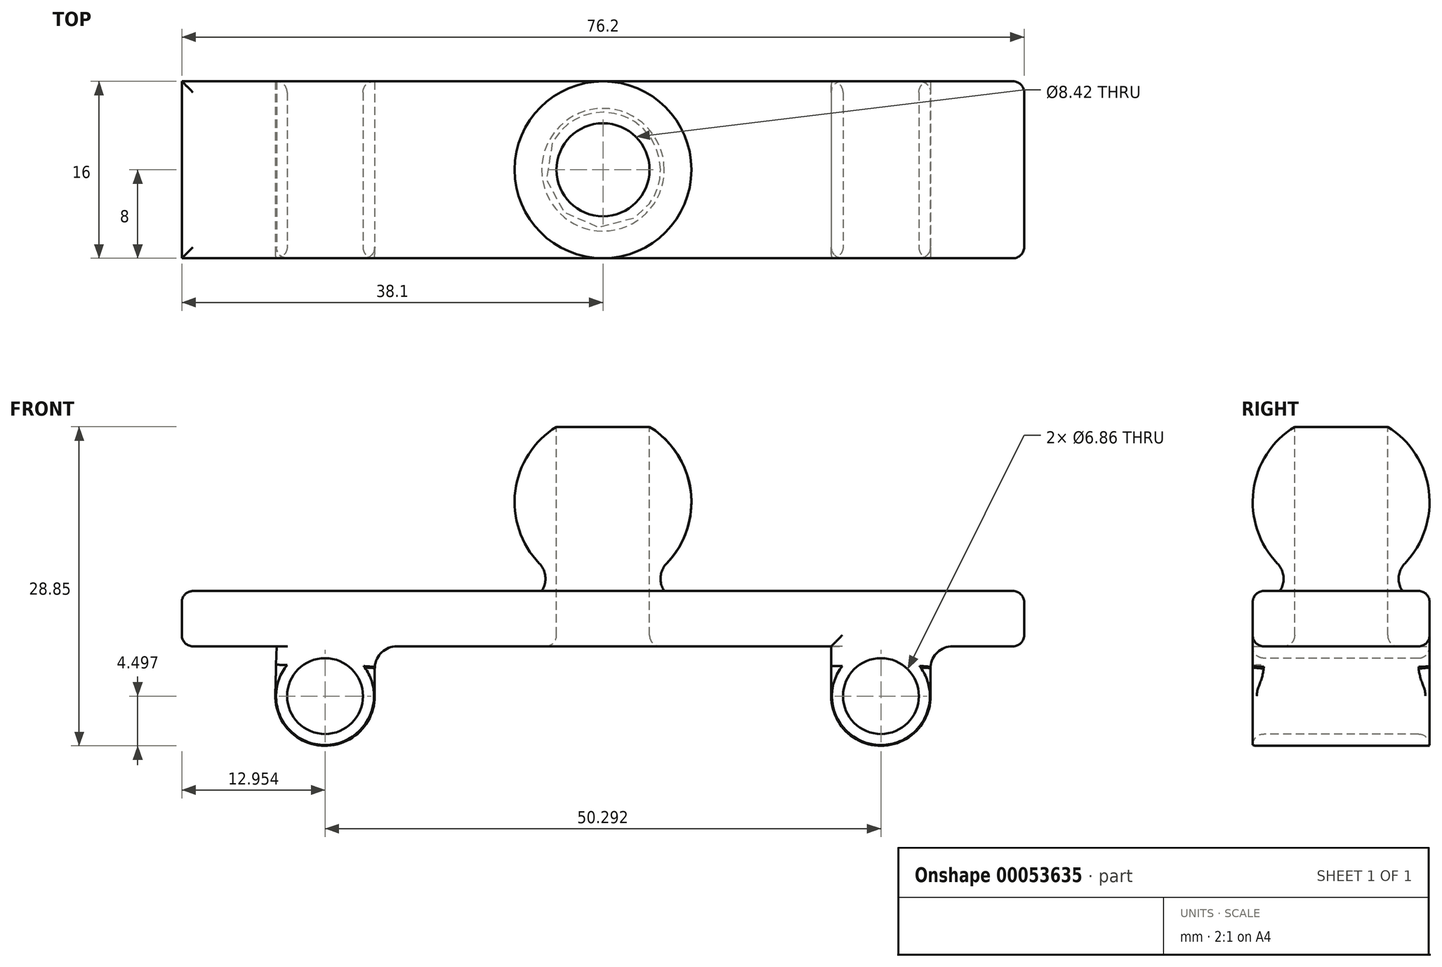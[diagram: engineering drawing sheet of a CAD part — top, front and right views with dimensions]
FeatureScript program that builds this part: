
annotation { "Feature Type Name" : "Feature", "Feature Type Description" : "" }
export const myFeature = defineFeature(function(context is Context, id is Id, definition is map)
    precondition{}
    {
        {
            var Q0;
            Q0=qCreatedBy(makeId("Front.planeOp"),FACE);
            var sketch = newSketch(context, id + "F0", { "sketchPlane" : qUnion([Q0])});
            skArc(sketch, "E0", {"start": v(0, 4.09) * mm, "mid": v(0.5, 4.1) * mm, "end": v(1, 4.15) * mm});
            skLineSegment(sketch, "E1", {"start": v(5.54, 4.04) * mm, "end": v(10.12, -2.8) * mm});
            skLineSegment(sketch, "E2", {"start": v(10.12, -2.8) * mm, "end": v(10.12, -5.91) * mm});
            skLineSegment(sketch, "E3", {"start": v(10.12, -5.91) * mm, "end": v(7.88, -5.91) * mm});
            skArc(sketch, "E4", {"start": v(7.88, -5.91) * mm, "mid": v(6.7, 0.67) * mm, "end": v(1, 4.15) * mm});
            skLineSegment(sketch, "E5", {"start": v(0, 10.09) * mm, "end": v(7.75, 10.09) * mm, "construction": true});
            skPoint(sketch, "E6", {"position": v(0, 20.09) * mm});
            skPoint(sketch, "E7", {"position": v(0, 10.09) * mm});
            skPoint(sketch, "E8.orphan", {"position": v(-7.75, 10.09) * mm});
            skPoint(sketch, "E9.orphan", {"position": v(0, -5.91) * mm});
            skLineSegment(sketch, "E10", {"start": v(0, 20.09) * mm, "end": v(0, 4.09) * mm});
            skArc(sketch, "E11.trimOffspring", {"start": v(5.76, 6.54) * mm, "mid": v(7.36, 15.22) * mm, "end": v(0, 20.09) * mm});
            skLineSegment(sketch, "E12", {"start": v(0, 4.09) * mm, "end": v(0, -5.91) * mm, "construction": true});
            skPoint(sketch, "E13.visualSharp", {"position": v(4.56, 5.5) * mm});
            skArc(sketch, "E13.filletArc", {"start": v(5.76, 6.54) * mm, "mid": v(5.21, 5.33) * mm, "end": v(5.54, 4.04) * mm});
            skSolve(sketch);
        }
        {
            var Q0;
            Q0=qSketchRegion(id+"F0",true);
            var Q1;
            Q1=sQuery(id+"F0.wireOp",EDGE,"E12");
            revolve(context, id + "F1", {"entities" : qUnion([Q0]), "axis" : qUnion([Q1]), "revolveType" : RevolveType.FULL});
        }
        {
            var Q0;
            Q0=qCreatedBy(makeId("Top.planeOp"),FACE);
            var sketch = newSketch(context, id + "F2", { "sketchPlane" : qUnion([Q0])});
            skCircle(sketch, "E14", {"center": v(0, 0) * mm, "radius": 4.2 * mm});
            skSolve(sketch);
        }
        {
            var Q0;
            Q0=qSketchRegion(id+"F2",true);
            extrude(context, id + "F3", {"entities" : qUnion([Q0]), "operationType" : NewBodyOperationType.REMOVE, "endBound" : BoundingType.SYMMETRIC, "oppositeDirection" : true, "depth" : 50 * mm});
        }
        {
            var Q0;
            Q0=qCreatedBy(makeId("Right.planeOp"),FACE);
            var sketch = newSketch(context, id + "F4", { "sketchPlane" : qUnion([Q0])});
            skLineSegment(sketch, "E15.bottom", {"start": v(1, -5.91) * mm, "end": v(-1, -5.91) * mm});
            skLineSegment(sketch, "E15.left", {"start": v(1, -5.91) * mm, "end": v(1, -0.91) * mm});
            skLineSegment(sketch, "E15.right", {"start": v(-1, -5.91) * mm, "end": v(-1, -0.91) * mm});
            skArc(sketch, "E16", {"start": v(1, -0.91) * mm, "mid": v(0, 0.09) * mm, "end": v(-1, -0.91) * mm});
            skSolve(sketch);
        }
        {
            var Q0;
            Q0=qSketchRegion(id+"F4",true);
            extrude(context, id + "F5", {"entities" : qUnion([Q0]), "operationType" : NewBodyOperationType.REMOVE, "endBound" : BoundingType.SYMMETRIC, "oppositeDirection" : true, "depth" : 25 * mm});
        }
        {
            var Q0;
            Q0=qCreatedBy(makeId("Front.planeOp"),FACE);
            var sketch = newSketch(context, id + "F6", { "sketchPlane" : qUnion([Q0])});
            skLineSegment(sketch, "E17.bottom", {"start": v(-34.6, 4.04) * mm, "end": v(25.65, 4.04) * mm});
            skLineSegment(sketch, "E17.top", {"start": v(-34.6, -16.9) * mm, "end": v(25.65, -16.9) * mm});
            skLineSegment(sketch, "E17.left", {"start": v(-34.6, 4.04) * mm, "end": v(-34.6, -16.9) * mm});
            skLineSegment(sketch, "E17.right", {"start": v(25.65, 4.04) * mm, "end": v(25.65, -16.9) * mm});
            skSolve(sketch);
        }
        {
            var Q0;
            Q0 = qSketchRegion(id + "F6", true);
            extrude(context, id + "F7", {"entities" : qUnion([Q0]), "operationType" : NewBodyOperationType.REMOVE, "endBound" : BoundingType.SYMMETRIC, "oppositeDirection" : true, "depth" : 25 * mm});
        }
        {
            var Q0;
            Q0=makeQuery(id+"F7.boolean.opBoolean","COPY",FACE,{"derivedFrom":makeQuery(id+"F7.opExtrude","SWEPT_FACE",FACE,{"disambiguationData":[OSD([sQuery(id+"F6.wireOp",EDGE,"E17.bottom")])]})});
            var sketch = newSketch(context, id + "F8", { "sketchPlane" : qUnion([Q0])});
            skLineSegment(sketch, "E18.rect.bottom", {"start": v(38.1, -8) * mm, "end": v(-38.1, -8) * mm});
            skLineSegment(sketch, "E18.rect.top", {"start": v(38.1, 8) * mm, "end": v(-38.1, 8) * mm});
            skLineSegment(sketch, "E18.rect.left", {"start": v(38.1, -8) * mm, "end": v(38.1, 8) * mm});
            skLineSegment(sketch, "E18.rect.right", {"start": v(-38.1, -8) * mm, "end": v(-38.1, 8) * mm});
            skPoint(sketch, "E18.rect.middle", {"position": v(0, 0) * mm});
            skSolve(sketch);
        }
        {
            var Q0;
            Q0 = qSketchRegion(id + "F8", true);
            extrude(context, id + "F9", {"entities" : qUnion([Q0]), "operationType" : NewBodyOperationType.ADD, "depth" : 5 * mm});
        }
        {
            var Q0;
            Q0=makeQuery(id+"F9.opExtrude","SWEPT_FACE",FACE,{"disambiguationData":[OSD([sQuery(id+"F8.wireOp",EDGE,"E18.rect.top")])]});
            var sketch = newSketch(context, id + "F10", { "sketchPlane" : qUnion([Q0])});
            skCircle(sketch, "E19", {"center": v(-25.15, -5.46) * mm, "radius": 3.43 * mm});
            skCircle(sketch, "E20", {"center": v(25.15, -5.46) * mm, "radius": 3.43 * mm});
            skLineSegment(sketch, "E21", {"start": v(-25.15, -5.46) * mm, "end": v(25.15, -5.46) * mm, "construction": true});
            skPoint(sketch, "E22", {"position": v(0, -5.46) * mm});
            skArc(sketch, "E23", {"start": v(-29.64, -5.34) * mm, "mid": v(-25.2, -9.96) * mm, "end": v(-20.65, -5.46) * mm});
            skArc(sketch, "E24", {"start": v(20.65, -5.46) * mm, "mid": v(25.16, -9.96) * mm, "end": v(29.65, -5.43) * mm});
            skLineSegment(sketch, "E25", {"start": v(-29.64, -5.34) * mm, "end": v(-29.53, -0.96) * mm});
            skLineSegment(sketch, "E26", {"start": v(-20.65, -5.46) * mm, "end": v(-20.65, -0.96) * mm});
            skLineSegment(sketch, "E27", {"start": v(20.65, -5.46) * mm, "end": v(20.65, -0.96) * mm});
            skLineSegment(sketch, "E28", {"start": v(-29.53, -0.96) * mm, "end": v(-20.65, -0.96) * mm});
            skLineSegment(sketch, "E29", {"start": v(20.65, -0.96) * mm, "end": v(29.61, -0.96) * mm});
            skLineSegment(sketch, "E30", {"start": v(29.65, -5.43) * mm, "end": v(29.61, -0.96) * mm});
            skSolve(sketch);
        }
        {
            var Q0;
            Q0 = qSketchRegion(id + "F10", true);
            extrude(context, id + "F11", {"entities" : qUnion([Q0]), "oppositeDirection" : true, "depth" : 16 * mm});
        }
        {
            var Q0;
            Q0=makeQuery(id+"F11.opExtrude","SWEPT_BODY",BODY,{"disambiguationData":[OSD([sQuery(id+"F10.wireOp",EDGE,"E19"),sQuery(id+"F10.wireOp",EDGE,"E23"),sQuery(id+"F10.wireOp",EDGE,"E25"),sQuery(id+"F10.wireOp",EDGE,"E26"),sQuery(id+"F10.wireOp",EDGE,"E28")])]});
            var Q1;
            Q1=makeQuery(id+"F1.opRevolve","SWEPT_BODY",BODY,{"disambiguationData":[OSD([sQuery(id+"F0.wireOp",EDGE,"E0"),sQuery(id+"F0.wireOp",EDGE,"E1"),sQuery(id+"F0.wireOp",EDGE,"E2"),sQuery(id+"F0.wireOp",EDGE,"E3"),sQuery(id+"F0.wireOp",EDGE,"E4"),sQuery(id+"F0.wireOp",EDGE,"E10"),sQuery(id+"F0.wireOp",EDGE,"E11.trimOffspring"),sQuery(id+"F0.wireOp",EDGE,"E13.filletArc")])]});
            booleanBodies(context, id + "F12", {"operationType" : BooleanOperationType.UNION, "tools" : qUnion([Q0, Q1])});
        }
        {
            var Q0;
            Q0=makeQuery(id+"F11.opExtrude","SWEPT_BODY",BODY,{"disambiguationData":[OSD([sQuery(id+"F10.wireOp",EDGE,"E20"),sQuery(id+"F10.wireOp",EDGE,"E24"),sQuery(id+"F10.wireOp",EDGE,"E27"),sQuery(id+"F10.wireOp",EDGE,"E29"),sQuery(id+"F10.wireOp",EDGE,"E30")])]});
            var Q1;
            Q1=makeQuery(id+"F11.opExtrude","SWEPT_BODY",BODY,{"disambiguationData":[OSD([sQuery(id+"F10.wireOp",EDGE,"E19"),sQuery(id+"F10.wireOp",EDGE,"E23"),sQuery(id+"F10.wireOp",EDGE,"E25"),sQuery(id+"F10.wireOp",EDGE,"E26"),sQuery(id+"F10.wireOp",EDGE,"E28")])]});
            booleanBodies(context, id + "F13", {"operationType" : BooleanOperationType.UNION, "tools" : qUnion([Q0, Q1])});
        }
        {
            var Q0;
            Q0=makeQuery(id+"F11.opExtrude","SWEPT_EDGE",EDGE,{"disambiguationData":[OSD([sQuery(id+"F8.wireOp",EDGE,"E18.rect.top"),sQuery(id+"F10.wireOp",EDGE,"E25"),sQuery(id+"F10.wireOp",EDGE,"E28")])]});
            var Q1;
            Q1=makeQuery(id+"F11.opExtrude","SWEPT_EDGE",EDGE,{"disambiguationData":[OSD([sQuery(id+"F8.wireOp",EDGE,"E18.rect.top"),sQuery(id+"F10.wireOp",EDGE,"E26"),sQuery(id+"F10.wireOp",EDGE,"E28")])]});
            var Q2;
            Q2=makeQuery(id+"F11.opExtrude","SWEPT_EDGE",EDGE,{"disambiguationData":[OSD([sQuery(id+"F8.wireOp",EDGE,"E18.rect.top"),sQuery(id+"F10.wireOp",EDGE,"E27"),sQuery(id+"F10.wireOp",EDGE,"E29")])]});
            var Q3;
            Q3=makeQuery(id+"F11.opExtrude","SWEPT_EDGE",EDGE,{"disambiguationData":[OSD([sQuery(id+"F8.wireOp",EDGE,"E18.rect.top"),sQuery(id+"F10.wireOp",EDGE,"E29"),sQuery(id+"F10.wireOp",EDGE,"E30")])]});
            fillet(context, id + "F14", {"entities" : qUnion([Q0, Q1, Q2, Q3]), "radius" : 2 * mm, "tangentPropagation" : true, "allowEdgeOverflow" : false});
        }
        {
            var Q0;
            Q0=makeQuery(id+"F11.opExtrude","CAP_EDGE",EDGE,{"disambiguationData":[OSD([sQuery(id+"F10.wireOp",EDGE,"E20")])],"isStart":false});
            var Q1;
            Q1=makeQuery(id+"F11.opExtrude","CAP_EDGE",EDGE,{"disambiguationData":[OSD([sQuery(id+"F10.wireOp",EDGE,"E19")])],"isStart":false});
            var Q2;
            Q2=makeQuery(id+"F11.opExtrude","CAP_EDGE",EDGE,{"disambiguationData":[OSD([sQuery(id+"F10.wireOp",EDGE,"E20")])],"isStart":true});
            var Q3;
            Q3=makeQuery(id+"F11.opExtrude","CAP_EDGE",EDGE,{"disambiguationData":[OSD([sQuery(id+"F10.wireOp",EDGE,"E19")])],"isStart":true});
            fillet(context, id + "F15", {"entities" : qUnion([Q0, Q1, Q2, Q3]), "radius" : 1 * mm, "tangentPropagation" : true, "allowEdgeOverflow" : false});
        }
        {
            var Q0;
            {var subQ0=sQuery(id+"F8.wireOp",EDGE,"E18.rect.left");var subQ1=sQuery(id+"F8.wireOp",EDGE,"E18.rect.top");var subQ2=sQuery(id+"F8.wireOp",EDGE,"E18.rect.bottom");var subQ3=sQuery(id+"F8.wireOp",EDGE,"E18.rect.right");Q0=makeQuery(id+"F9.boolean.opBoolean","SPLIT",FACE,{"disambiguationData":[TD([makeQuery(id+"F1.opRevolve","SWEPT_FACE",FACE,{"disambiguationData":[OSD([sQuery(id+"F0.wireOp",EDGE,"E13.filletArc")])]})])],"derivedFrom":makeQuery(id+"F9.opExtrude","CAP_FACE",FACE,{"disambiguationData":[OSD([subQ2,subQ1,subQ0,subQ3])],"isStart":true})});}
            var sketch = newSketch(context, id + "F16", { "sketchPlane" : qUnion([Q0])});
            skCircle(sketch, "E31", {"center": v(0, 0) * mm, "radius": 4.2 * mm});
            skSolve(sketch);
        }
        {
            var Q0;
            Q0 = qSketchRegion(id + "F16", true);
            extrude(context, id + "F17", {"entities" : qUnion([Q0]), "operationType" : NewBodyOperationType.REMOVE, "endBound" : BoundingType.THROUGH_ALL, "oppositeDirection" : true, "depth" : 25 * mm});
        }
        {
            var Q0;
            Q0=makeQuery(id+"F9.opExtrude","CAP_EDGE",EDGE,{"disambiguationData":[OSD([sQuery(id+"F8.wireOp",EDGE,"E18.rect.top")])],"isStart":true});
            var Q1;
            Q1=makeQuery(id+"F9.opExtrude","CAP_EDGE",EDGE,{"disambiguationData":[OSD([sQuery(id+"F8.wireOp",EDGE,"E18.rect.left")])],"isStart":true});
            var Q2;
            Q2=makeQuery(id+"F9.opExtrude","CAP_EDGE",EDGE,{"disambiguationData":[OSD([sQuery(id+"F8.wireOp",EDGE,"E18.rect.bottom")])],"isStart":true});
            var Q3;
            Q3=makeQuery(id+"F9.opExtrude","CAP_EDGE",EDGE,{"disambiguationData":[OSD([sQuery(id+"F8.wireOp",EDGE,"E18.rect.right")])],"isStart":true});
            var Q4;
            {var subQ1=sQuery(id+"F10.wireOp",EDGE,"E26");var subQ3=sQuery(id+"F8.wireOp",EDGE,"E18.rect.top");var subQ5=sQuery(id+"F8.wireOp",EDGE,"E18.rect.left");var subQ7=makeQuery(id+"F11.opExtrude","SWEPT_FACE",FACE,{"disambiguationData":[OSD([subQ1])]});Q4=makeQuery(id+"F13.opBoolean","SPLIT",EDGE,{"disambiguationData":[TD([subQ7])],"derivedFrom":makeQuery(id+"F12.opBoolean","SPLIT",EDGE,{"disambiguationData":[TD([makeQuery(id+"F9.opExtrude","SWEPT_FACE",FACE,{"disambiguationData":[OSD([subQ5])]})])],"derivedFrom":makeQuery(id+"F9.opExtrude","CAP_EDGE",EDGE,{"disambiguationData":[OSD([subQ3])],"isStart":false})})});}
            var Q5;
            {var subQ3=sQuery(id+"F8.wireOp",EDGE,"E18.rect.left");var subQ4=makeQuery(id+"F9.opExtrude","SWEPT_FACE",FACE,{"disambiguationData":[OSD([subQ3])]});var subQ5=sQuery(id+"F8.wireOp",EDGE,"E18.rect.top");Q5=makeQuery(id+"F13.opBoolean","SPLIT",EDGE,{"disambiguationData":[TD([subQ4])],"derivedFrom":makeQuery(id+"F12.opBoolean","SPLIT",EDGE,{"disambiguationData":[TD([subQ4])],"derivedFrom":makeQuery(id+"F9.opExtrude","CAP_EDGE",EDGE,{"disambiguationData":[OSD([subQ5])],"isStart":false})})});}
            var Q6;
            Q6=makeQuery(id+"F9.opExtrude","SWEPT_EDGE",EDGE,{"disambiguationData":[OSD([sQuery(id+"F8.wireOp",EDGE,"E18.rect.top"),sQuery(id+"F8.wireOp",EDGE,"E18.rect.left")])]});
            var Q7;
            Q7=makeQuery(id+"F9.opExtrude","CAP_EDGE",EDGE,{"disambiguationData":[OSD([sQuery(id+"F8.wireOp",EDGE,"E18.rect.left")])],"isStart":false});
            var Q8;
            Q8=makeQuery(id+"F9.opExtrude","SWEPT_EDGE",EDGE,{"disambiguationData":[OSD([sQuery(id+"F8.wireOp",EDGE,"E18.rect.bottom"),sQuery(id+"F8.wireOp",EDGE,"E18.rect.left")])]});
            var Q9;
            {var subQ2=sQuery(id+"F8.wireOp",EDGE,"E18.rect.left");var subQ3=makeQuery(id+"F9.opExtrude","SWEPT_FACE",FACE,{"disambiguationData":[OSD([subQ2])]});var subQ4=sQuery(id+"F8.wireOp",EDGE,"E18.rect.bottom");Q9=makeQuery(id+"F13.opBoolean","SPLIT",EDGE,{"disambiguationData":[TD([subQ3])],"derivedFrom":makeQuery(id+"F12.opBoolean","SPLIT",EDGE,{"disambiguationData":[TD([subQ3])],"derivedFrom":makeQuery(id+"F9.opExtrude","CAP_EDGE",EDGE,{"disambiguationData":[OSD([subQ4])],"isStart":false})})});}
            var Q10;
            Q10=makeQuery(id+"F9.opExtrude","CAP_EDGE",EDGE,{"disambiguationData":[OSD([sQuery(id+"F8.wireOp",EDGE,"E18.rect.right")])],"isStart":false});
            var Q11;
            {var subQ1=sQuery(id+"F10.wireOp",EDGE,"E26");var subQ12=sQuery(id+"F8.wireOp",EDGE,"E18.rect.top");var subQ14=sQuery(id+"F8.wireOp",EDGE,"E18.rect.bottom");var subQ16=makeQuery(id+"F11.opExtrude","SWEPT_FACE",FACE,{"disambiguationData":[OSD([subQ1])]});var subQ17=sQuery(id+"F8.wireOp",EDGE,"E18.rect.left");Q11=makeQuery(id+"F17.boolean.opBoolean","INTERSECT",EDGE,{"derivedFrom":[makeQuery(id+"F13.opBoolean","SPLIT",FACE,{"disambiguationData":[TD([subQ16])],"derivedFrom":makeQuery(id+"F12.opBoolean","SPLIT",FACE,{"disambiguationData":[TD([makeQuery(id+"F9.opExtrude","SWEPT_FACE",FACE,{"disambiguationData":[OSD([subQ17])]})])],"derivedFrom":makeQuery(id+"F9.opExtrude","CAP_FACE",FACE,{"disambiguationData":[OSD([subQ14,subQ12,subQ17,sQuery(id+"F8.wireOp",EDGE,"E18.rect.right")])],"isStart":false})})}),makeQuery(id+"F17.opExtrude","SWEPT_FACE",FACE,{"disambiguationData":[OSD([sQuery(id+"F16.wireOp",EDGE,"E31")])]})]});}
            fillet(context, id + "F18", {"entities" : qUnion([Q0, Q1, Q2, Q3, Q4, Q5, Q6, Q7, Q8, Q9, Q10, Q11]), "radius" : 1 * mm, "tangentPropagation" : true, "allowEdgeOverflow" : false});
        }
    });
